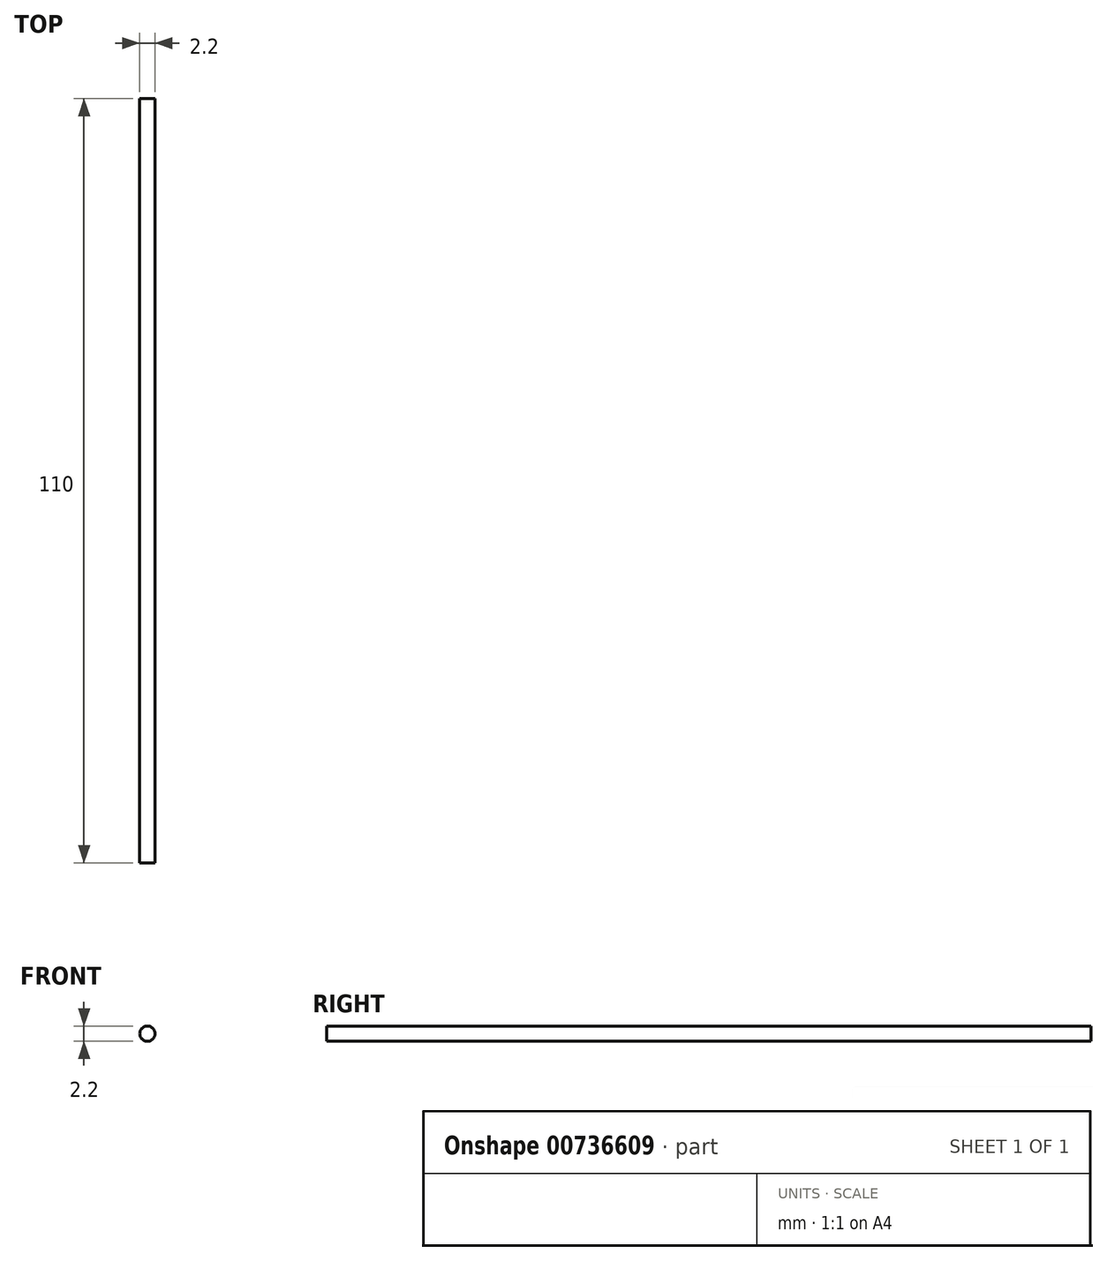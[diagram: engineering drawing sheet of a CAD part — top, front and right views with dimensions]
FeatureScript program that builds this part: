
annotation { "Feature Type Name" : "Feature", "Feature Type Description" : "" }
export const myFeature = defineFeature(function(context is Context, id is Id, definition is map)
    precondition{}
    {
        {
            var Q0;
            Q0=qCreatedBy(makeId("Front.planeOp"),FACE);
            var sketch = newSketch(context, id + "F0", { "sketchPlane" : qUnion([Q0])});
            skCircle(sketch, "E0", {"center": v(0, 0) * mm, "radius": 1.1 * mm});
            skSolve(sketch);
        }
        {
            var Q0;
            Q0=qSketchRegion(id+"F0",true);
            extrude(context, id + "F1", {"entities" : qUnion([Q0]), "depth" : 110 * mm, "offsetDistance" : 25 * mm, "symmetric" : true});
        }
    });
